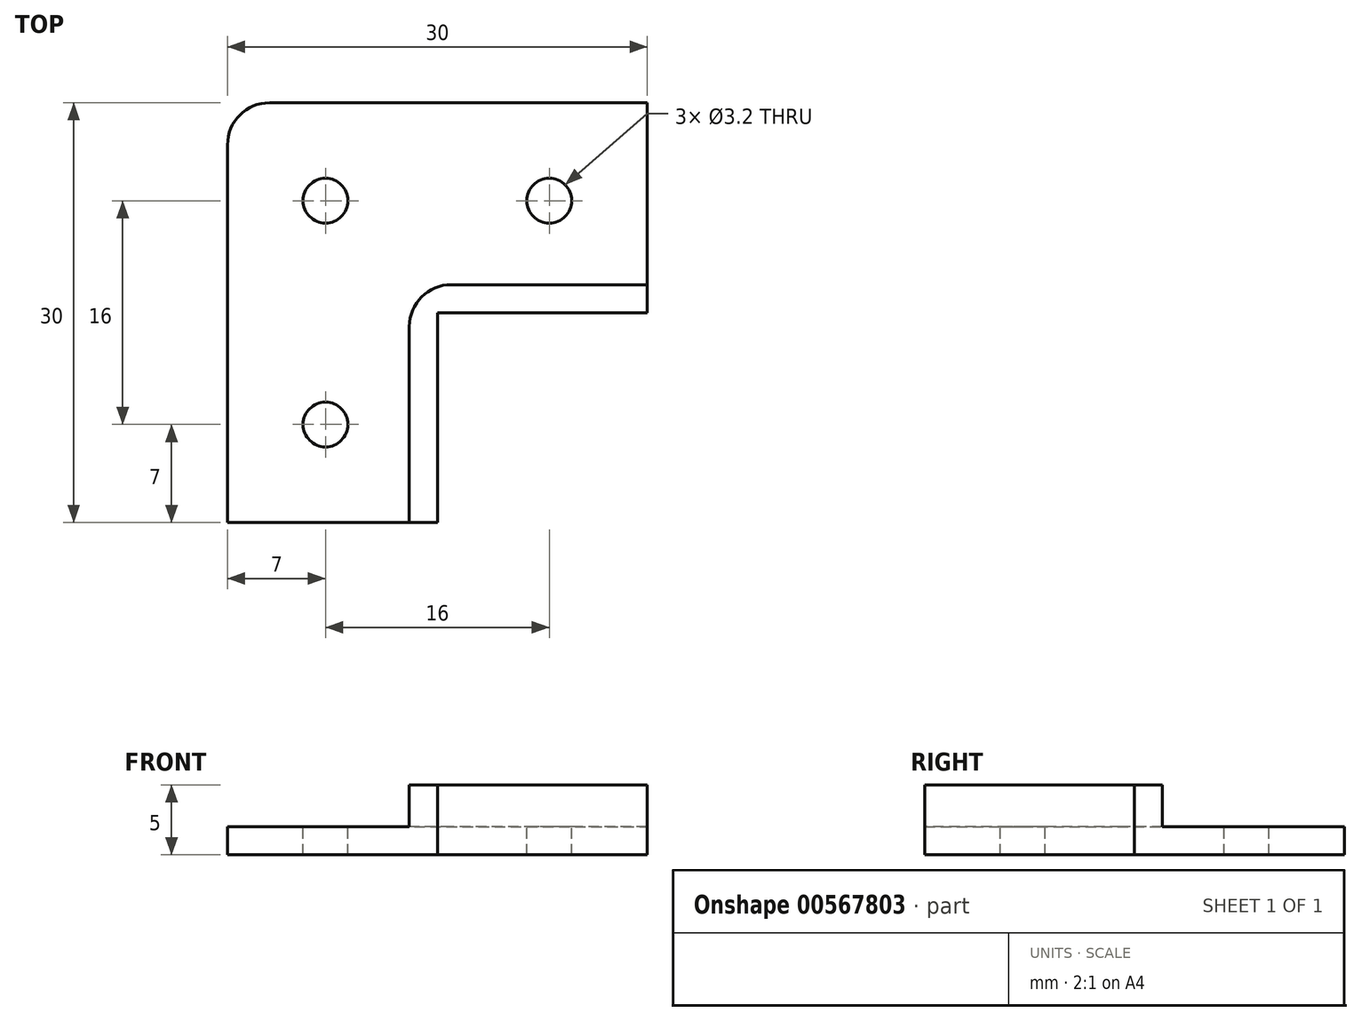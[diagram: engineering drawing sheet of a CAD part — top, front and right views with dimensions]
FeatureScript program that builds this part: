
annotation { "Feature Type Name" : "Feature", "Feature Type Description" : "" }
export const myFeature = defineFeature(function(context is Context, id is Id, definition is map)
    precondition{}
    {
        {
            var Q0;
            Q0=qCreatedBy(makeId("Top.planeOp"),FACE);
            var sketch = newSketch(context, id + "F0", { "sketchPlane" : qUnion([Q0])});
            skLineSegment(sketch, "E0", {"start": v(0, -15) * mm, "end": v(-15, -15) * mm});
            skLineSegment(sketch, "E1", {"start": v(-15, -15) * mm, "end": v(-15, 15) * mm});
            skLineSegment(sketch, "E2", {"start": v(-15, 15) * mm, "end": v(15, 15) * mm});
            skLineSegment(sketch, "E3", {"start": v(15, 15) * mm, "end": v(15, 0) * mm});
            skLineSegment(sketch, "E4", {"start": v(15, 0) * mm, "end": v(0, 0) * mm});
            skLineSegment(sketch, "E5", {"start": v(0, 0) * mm, "end": v(0, -15) * mm});
            skSolve(sketch);
        }
        {
            var Q0;
            Q0=makeQuery(id+"F0.imprint","IMPRINT",FACE,{"disambiguationData":[TD([[makeQuery(id+"F0.imprint","IMPRINT",EDGE,{"derivedFrom":sQuery(id+"F0.wireOp",EDGE,"E0")}),-1.0]])]});
            extrude(context, id + "F1", {"entities" : qUnion([Q0]), "depth" : 2 * mm, "offsetDistance" : 25 * mm});
        }
        {
            var Q0;
            Q0=makeQuery(id+"F1.opExtrude","CAP_FACE",FACE,{"disambiguationData":[OSD([sQuery(id+"F0.wireOp",EDGE,"E0"),sQuery(id+"F0.wireOp",EDGE,"E1"),sQuery(id+"F0.wireOp",EDGE,"E2"),sQuery(id+"F0.wireOp",EDGE,"E3"),sQuery(id+"F0.wireOp",EDGE,"E4"),sQuery(id+"F0.wireOp",EDGE,"E5")])],"isStart":false});
            var sketch = newSketch(context, id + "F2", { "sketchPlane" : qUnion([Q0])});
            skLineSegment(sketch, "E6", {"start": v(15, 2) * mm, "end": v(-2, 2) * mm});
            skLineSegment(sketch, "E7", {"start": v(-2, 2) * mm, "end": v(-2, -15) * mm});
            skLineSegment(sketch, "E8", {"start": v(-2, -15) * mm, "end": v(0, -15) * mm});
            skLineSegment(sketch, "E9", {"start": v(0, -15) * mm, "end": v(0, 0) * mm});
            skLineSegment(sketch, "E10", {"start": v(0, 0) * mm, "end": v(15, 0) * mm});
            skLineSegment(sketch, "E11", {"start": v(15, 0) * mm, "end": v(15, 2) * mm});
            skSolve(sketch);
        }
        {
            var Q0;
            Q0=makeQuery(id+"F2.imprint","IMPRINT",FACE,{"disambiguationData":[TD([[makeQuery(id+"F2.imprint","IMPRINT",EDGE,{"derivedFrom":sQuery(id+"F2.wireOp",EDGE,"E6")}),1.0]])]});
            extrude(context, id + "F3", {"entities" : qUnion([Q0]), "operationType" : NewBodyOperationType.ADD, "depth" : 3 * mm, "offsetDistance" : 25 * mm});
        }
        {
            var Q0;
            Q0=makeQuery(id+"F1.opExtrude","CAP_FACE",FACE,{"disambiguationData":[OSD([sQuery(id+"F0.wireOp",EDGE,"E0"),sQuery(id+"F0.wireOp",EDGE,"E1"),sQuery(id+"F0.wireOp",EDGE,"E2"),sQuery(id+"F0.wireOp",EDGE,"E3"),sQuery(id+"F0.wireOp",EDGE,"E4"),sQuery(id+"F0.wireOp",EDGE,"E5")])],"isStart":false});
            var sketch = newSketch(context, id + "F4", { "sketchPlane" : qUnion([Q0])});
            skPoint(sketch, "E12", {"position": v(-8, 8) * mm});
            skPoint(sketch, "E13", {"position": v(8, 8) * mm});
            skPoint(sketch, "E14", {"position": v(-8, -8) * mm});
            skSolve(sketch);
        }
        {
            var Q0;
            Q0=sQuery(id+"F4.wireOp",VERTEX,"E12");
            var Q1;
            Q1=sQuery(id+"F4.wireOp",VERTEX,"E13");
            var Q2;
            Q2=sQuery(id+"F4.wireOp",VERTEX,"E14");
            var Q3;
            Q3=makeQuery(id+"F1.opExtrude","SWEPT_BODY",BODY,{"disambiguationData":[OSD([sQuery(id+"F0.wireOp",EDGE,"E0"),sQuery(id+"F0.wireOp",EDGE,"E1"),sQuery(id+"F0.wireOp",EDGE,"E2"),sQuery(id+"F0.wireOp",EDGE,"E3"),sQuery(id+"F0.wireOp",EDGE,"E4"),sQuery(id+"F0.wireOp",EDGE,"E5")])]});
            hole(context, id + "F5", {"style" : HoleStyle.SIMPLE, "endStyle" : HoleEndStyle.THROUGH, "holeDiameter" : 3.2 * mm, "isTappedThrough" : true, "tappedDepth" : 12 * mm, "tapClearance" : 3, "locations" : qUnion([Q0, Q1, Q2]), "scope" : qUnion([Q3])});
        }
        {
            var Q0;
            Q0=makeQuery(id+"F1.opExtrude","SWEPT_EDGE",EDGE,{"disambiguationData":[OSD([sQuery(id+"F0.wireOp",EDGE,"E1"),sQuery(id+"F0.wireOp",EDGE,"E2")])]});
            var Q1;
            Q1=makeQuery(id+"F3.opExtrude","SWEPT_EDGE",EDGE,{"disambiguationData":[OSD([sQuery(id+"F2.wireOp",EDGE,"E6"),sQuery(id+"F2.wireOp",EDGE,"E7")])]});
            fillet(context, id + "F6", {"entities" : qUnion([Q0, Q1]), "radius" : 3 * mm, "tangentPropagation" : true, "allowEdgeOverflow" : false});
        }
    });
